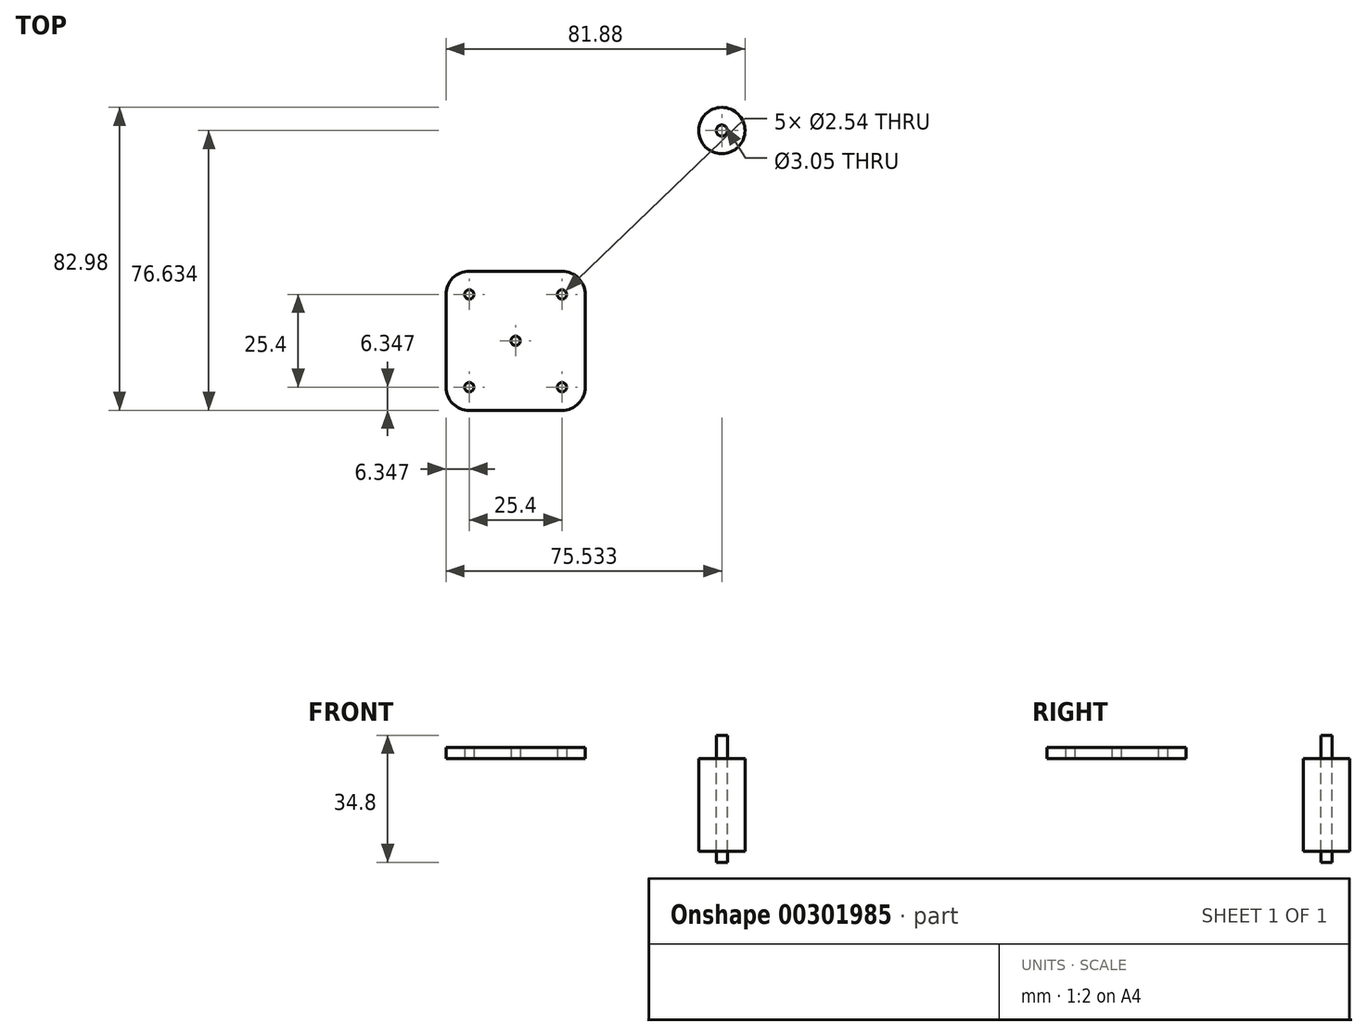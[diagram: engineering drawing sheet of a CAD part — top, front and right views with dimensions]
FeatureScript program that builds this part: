
annotation { "Feature Type Name" : "Feature", "Feature Type Description" : "" }
export const myFeature = defineFeature(function(context is Context, id is Id, definition is map)
    precondition{}
    {
        {
            var Q0;
            Q0=qCreatedBy(makeId("Top.planeOp"),FACE);
            var sketch = newSketch(context, id + "F0", { "sketchPlane" : qUnion([Q0])});
            skLineSegment(sketch, "E0.bottom", {"start": v(-45.91, -14.22) * mm, "end": v(-20.51, -14.22) * mm});
            skLineSegment(sketch, "E0.top", {"start": v(-45.91, -52.32) * mm, "end": v(-20.51, -52.32) * mm});
            skLineSegment(sketch, "E0.left", {"start": v(-52.26, -20.57) * mm, "end": v(-52.26, -45.97) * mm});
            skLineSegment(sketch, "E0.right", {"start": v(-14.16, -20.57) * mm, "end": v(-14.16, -45.97) * mm});
            skPoint(sketch, "E1.visualSharp", {"position": v(-52.26, -14.22) * mm});
            skArc(sketch, "E1.filletArc", {"start": v(-45.91, -14.22) * mm, "mid": v(-50.4, -16.08) * mm, "end": v(-52.26, -20.57) * mm});
            skPoint(sketch, "E2.visualSharp", {"position": v(-14.16, -14.22) * mm});
            skArc(sketch, "E2.filletArc", {"start": v(-14.16, -20.57) * mm, "mid": v(-16.02, -16.08) * mm, "end": v(-20.51, -14.22) * mm});
            skPoint(sketch, "E3.visualSharp", {"position": v(-14.16, -52.32) * mm});
            skArc(sketch, "E3.filletArc", {"start": v(-20.51, -52.32) * mm, "mid": v(-16.02, -50.46) * mm, "end": v(-14.16, -45.97) * mm});
            skPoint(sketch, "E4.visualSharp", {"position": v(-52.26, -52.32) * mm});
            skArc(sketch, "E4.filletArc", {"start": v(-52.26, -45.97) * mm, "mid": v(-50.4, -50.46) * mm, "end": v(-45.91, -52.32) * mm});
            skCircle(sketch, "E5", {"center": v(-33.21, -33.27) * mm, "radius": 1.27 * mm});
            skCircle(sketch, "E6", {"center": v(-20.51, -20.57) * mm, "radius": 1.27 * mm});
            skCircle(sketch, "E7", {"center": v(-45.91, -20.57) * mm, "radius": 1.27 * mm});
            skCircle(sketch, "E8", {"center": v(-45.91, -45.97) * mm, "radius": 1.27 * mm});
            skCircle(sketch, "E9", {"center": v(-20.51, -45.97) * mm, "radius": 1.27 * mm});
            skSolve(sketch);
        }
        {
            var Q0;
            Q0=makeQuery(id+"F0.imprint","IMPRINT",FACE,{"disambiguationData":[TD([[makeQuery(id+"F0.imprint","IMPRINT",EDGE,{"derivedFrom":sQuery(id+"F0.wireOp",EDGE,"E0.bottom")}),-1.0]])]});
            extrude(context, id + "F1", {"entities" : qUnion([Q0]), "depth" : 3.05 * mm});
        }
        {
            var Q0;
            Q0=qCreatedBy(makeId("Top.planeOp"),FACE);
            var sketch = newSketch(context, id + "F2", { "sketchPlane" : qUnion([Q0])});
            skCircle(sketch, "E10", {"center": v(23.27, 24.31) * mm, "radius": 6.35 * mm});
            skCircle(sketch, "E11", {"center": v(23.27, 24.31) * mm, "radius": 1.52 * mm});
            skSolve(sketch);
        }
        {
            var Q0;
            Q0=makeQuery(id+"F2.imprint","IMPRINT",FACE,{"disambiguationData":[TD([[makeQuery(id+"F2.imprint","IMPRINT",EDGE,{"derivedFrom":sQuery(id+"F2.wireOp",EDGE,"E11")}),1.0]])]});
            extrude(context, id + "F3", {"entities" : qUnion([Q0]), "depth" : 6.35 * mm});
        }
        {
            var Q0;
            Q0 = qSketchRegion(id + "F2", true);
            extrude(context, id + "F4", {"entities" : qUnion([Q0]), "operationType" : NewBodyOperationType.ADD, "oppositeDirection" : true, "depth" : 25.4 * mm});
        }
        {
            var Q0;
            Q0=makeQuery(id+"F3.opExtrude","CAP_FACE",FACE,{"disambiguationData":[OSD([sQuery(id+"F2.wireOp",EDGE,"E11")])],"isStart":false});
            extrude(context, id + "F5", {"entities" : qUnion([Q0]), "oppositeDirection" : true, "depth" : 34.8 * mm});
        }
    });
